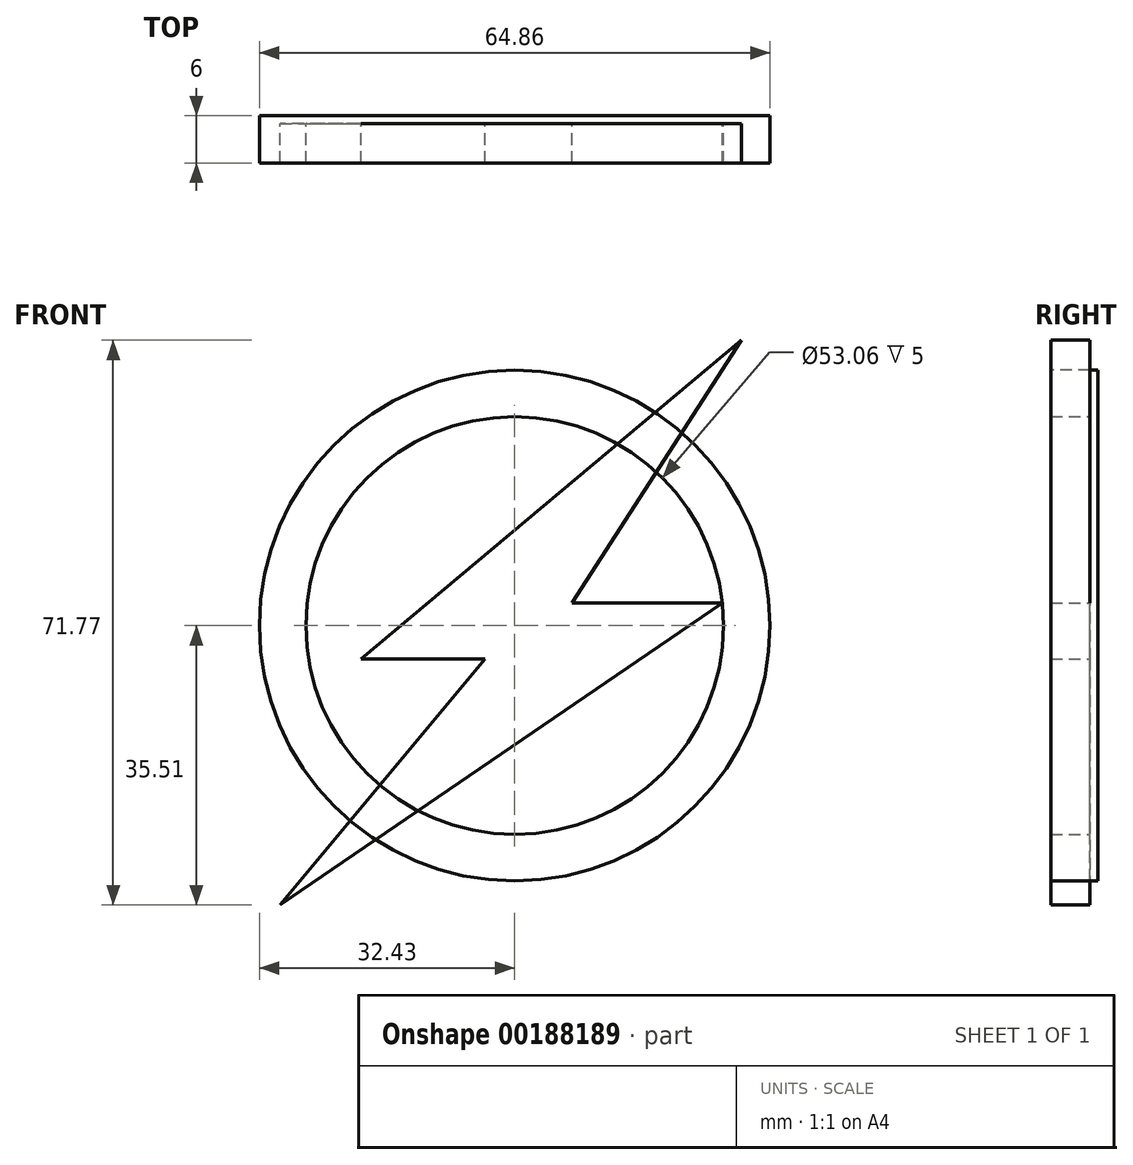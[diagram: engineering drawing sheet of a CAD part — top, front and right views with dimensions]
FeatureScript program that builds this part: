
annotation { "Feature Type Name" : "Feature", "Feature Type Description" : "" }
export const myFeature = defineFeature(function(context is Context, id is Id, definition is map)
    precondition{}
    {
        {
            var Q0;
            Q0=qCreatedBy(makeId("Front.planeOp"),FACE);
            var sketch = newSketch(context, id + "F0", { "sketchPlane" : qUnion([Q0])});
            skCircle(sketch, "E0", {"center": v(0, 0) * mm, "radius": 32.43 * mm});
            skSolve(sketch);
        }
        {
            var Q0;
            Q0 = qSketchRegion(id + "F0", true);
            extrude(context, id + "F1", {"entities" : qUnion([Q0]), "oppositeDirection" : true, "depth" : 1 * mm});
        }
        {
            var Q0;
            Q0=makeQuery(id+"F1.opExtrude","CAP_FACE",FACE,{"disambiguationData":[OSD([sQuery(id+"F0.wireOp",EDGE,"E0")])],"isStart":true});
            var sketch = newSketch(context, id + "F2", { "sketchPlane" : qUnion([Q0])});
            skCircle(sketch, "E1", {"center": v(0, 0) * mm, "radius": 26.53 * mm});
            skSolve(sketch);
        }
        {
            var Q0;
            Q0=makeQuery(id+"F2.imprint","IMPRINT",FACE,{"disambiguationData":[TD([[makeQuery(id+"F2.imprint","IMPRINT",EDGE,{"derivedFrom":sQuery(id+"F2.wireOp",EDGE,"E1")}),-1.0]])]});
            extrude(context, id + "F3", {"entities" : qUnion([Q0]), "operationType" : NewBodyOperationType.ADD, "depth" : 5 * mm});
        }
        {
            var Q0;
            Q0=makeQuery(id+"F1.opExtrude","CAP_FACE",FACE,{"disambiguationData":[OSD([sQuery(id+"F0.wireOp",EDGE,"E0")])],"isStart":true});
            var sketch = newSketch(context, id + "F4", { "sketchPlane" : qUnion([Q0])});
            skLineSegment(sketch, "E2", {"start": v(28.82, 36.26) * mm, "end": v(-19.53, -4.22) * mm});
            skLineSegment(sketch, "E3", {"start": v(-19.53, -4.22) * mm, "end": v(-3.79, -4.22) * mm});
            skLineSegment(sketch, "E4", {"start": v(-3.79, -4.22) * mm, "end": v(-29.83, -35.51) * mm});
            skLineSegment(sketch, "E5", {"start": v(-29.83, -35.51) * mm, "end": v(26.38, 2.85) * mm});
            skLineSegment(sketch, "E6", {"start": v(26.38, 2.85) * mm, "end": v(7.27, 2.85) * mm});
            skLineSegment(sketch, "E7", {"start": v(7.27, 2.85) * mm, "end": v(28.82, 36.26) * mm});
            skSolve(sketch);
        }
        {
            var Q0;
            {var subQ5=sQuery(id+"F4.wireOp",EDGE,"E3");Q0=makeQuery(id+"F4.imprint","IMPRINT",FACE,{"disambiguationData":[TD([[makeQuery(id+"F4.imprint","IMPRINT",EDGE,{"derivedFrom":subQ5}),1.0]])]});}
            var Q1;
            {var subQ0=sQuery(id+"F4.wireOp",EDGE,"E5");var subQ1=sQuery(id+"F4.wireOp",EDGE,"E4");var subQ2=makeQuery(id+"F4.imprint","INTERSECT",VERTEX,{"derivedFrom":[subQ1,subQ0]});Q1=makeQuery(id+"F4.imprint","IMPRINT",FACE,{"disambiguationData":[TD([[makeQuery(id+"F4.imprint","IMPRINT",EDGE,{"disambiguationData":[TD([[subQ2,1.0]])],"derivedFrom":subQ1}),1.0]])]});}
            var Q2;
            {var subQ0=sQuery(id+"F4.wireOp",EDGE,"E7");var subQ1=sQuery(id+"F4.wireOp",EDGE,"E2");var subQ2=makeQuery(id+"F4.imprint","INTERSECT",VERTEX,{"derivedFrom":[subQ1,subQ0]});Q2=makeQuery(id+"F4.imprint","IMPRINT",FACE,{"disambiguationData":[TD([[makeQuery(id+"F4.imprint","IMPRINT",EDGE,{"disambiguationData":[TD([[subQ2,-1.0]])],"derivedFrom":subQ1}),1.0]])]});}
            extrude(context, id + "F5", {"entities" : qUnion([Q0, Q1, Q2]), "depth" : 5 * mm});
        }
        {
            var Q0;
            Q0=makeQuery(id+"F3.opExtrude","CAP_FACE",FACE,{"disambiguationData":[OSD([sQuery(id+"F0.wireOp",EDGE,"E0"),sQuery(id+"F2.wireOp",EDGE,"E1")])],"isStart":false});
            var sketch = newSketch(context, id + "F6", { "sketchPlane" : qUnion([Q0])});
            skCircle(sketch, "E8", {"center": v(0, 32.43) * mm, "radius": 5.79 * mm});
            skCircle(sketch, "E9", {"center": v(0, 32.43) * mm, "radius": 9.44 * mm});
            skSolve(sketch);
        }
        {
            var Q0;
            {var subQ0=sQuery(id+"F6.wireOp",EDGE,"E8");var subQ1=makeQuery(id+"F3.opExtrude","CAP_EDGE",EDGE,{"disambiguationData":[OSD([sQuery(id+"F0.wireOp",EDGE,"E0")])],"isStart":false});var subQ2=makeQuery(id+"F6.imprint","INTERSECT",VERTEX,{"disambiguationData":[OD(0.0)],"derivedFrom":[subQ1,subQ0]});Q0=makeQuery(id+"F6.imprint","IMPRINT",FACE,{"disambiguationData":[TD([[makeQuery(id+"F6.imprint","IMPRINT",EDGE,{"disambiguationData":[TD([[subQ2,1.0]])],"derivedFrom":subQ0}),-1.0]])]});}
            extrude(context, id + "F7", {"entities" : qUnion([Q0]), "operationType" : NewBodyOperationType.ADD, "oppositeDirection" : true, "depth" : 6 * mm});
        }
    });
